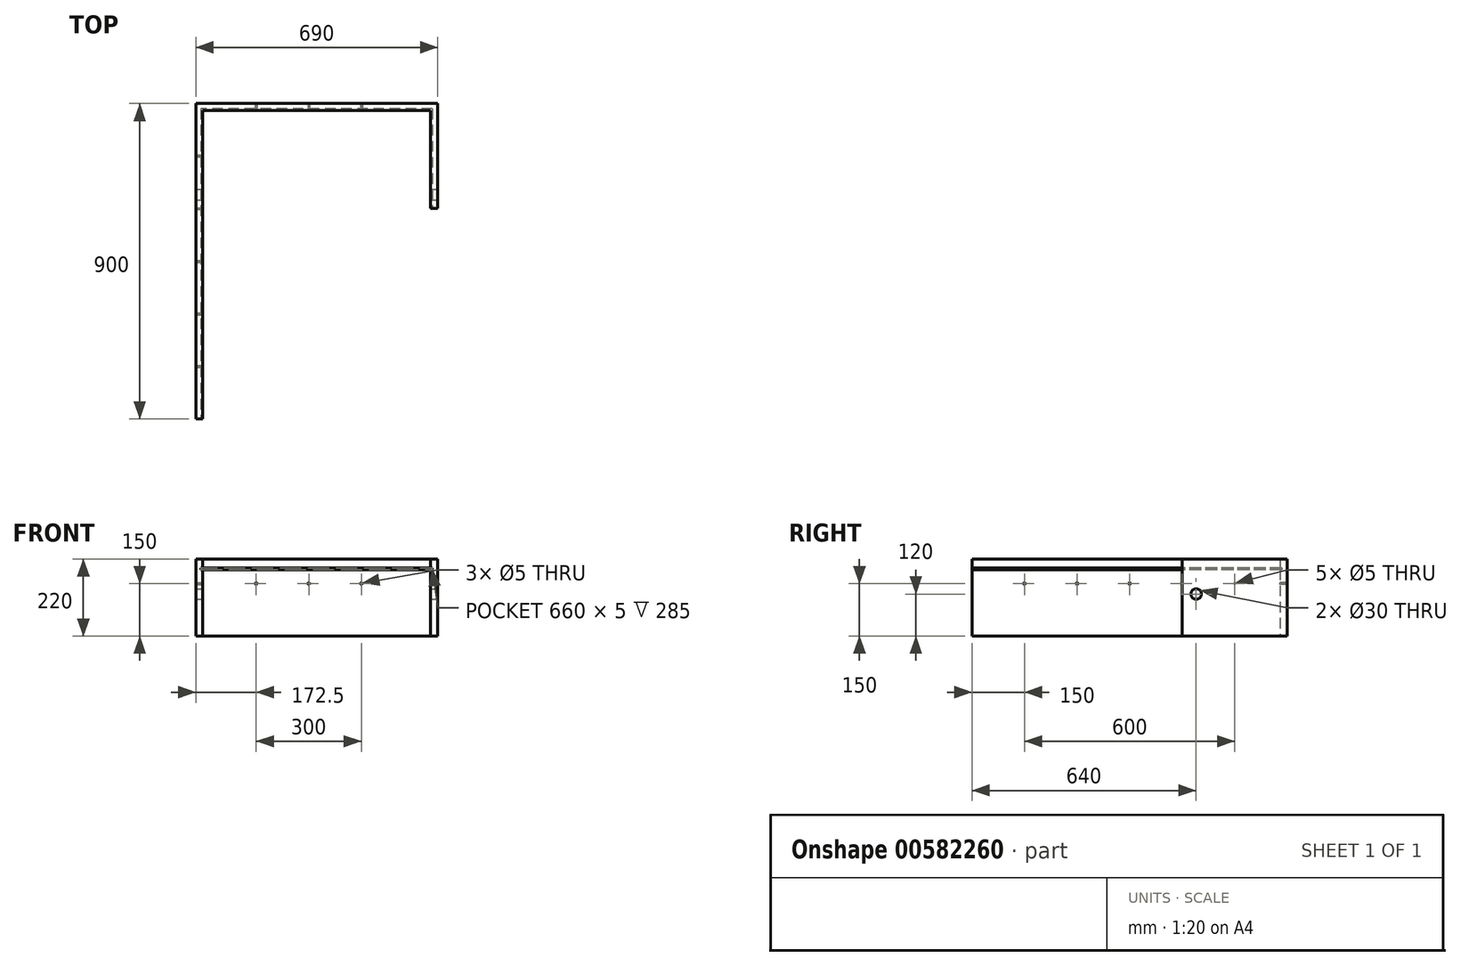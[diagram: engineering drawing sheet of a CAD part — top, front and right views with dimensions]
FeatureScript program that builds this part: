
annotation { "Feature Type Name" : "Feature", "Feature Type Description" : "" }
export const myFeature = defineFeature(function(context is Context, id is Id, definition is map)
    precondition{}
    {
        {
            var Q0;
            Q0=qCreatedBy(makeId("Top.planeOp"),FACE);
            var sketch = newSketch(context, id + "F0", { "sketchPlane" : qUnion([Q0])});
            skLineSegment(sketch, "E0.bottom", {"start": v(-325, -450) * mm, "end": v(-345, -450) * mm});
            skLineSegment(sketch, "E0.top", {"start": v(345, 450) * mm, "end": v(-345, 450) * mm});
            skLineSegment(sketch, "E0.left", {"start": v(345, 150) * mm, "end": v(345, 450) * mm});
            skLineSegment(sketch, "E0.right", {"start": v(-345, -450) * mm, "end": v(-345, 450) * mm});
            skPoint(sketch, "E0.middle", {"position": v(0, 0) * mm});
            skLineSegment(sketch, "E1.bottom", {"start": v(325, 430) * mm, "end": v(-325, 430) * mm});
            skLineSegment(sketch, "E1.left", {"start": v(325, 430) * mm, "end": v(325, 150) * mm});
            skLineSegment(sketch, "E1.right", {"start": v(-325, 430) * mm, "end": v(-325, -430) * mm});
            skLineSegment(sketch, "E2", {"start": v(345, 150) * mm, "end": v(325, 150) * mm});
            skLineSegment(sketch, "E3", {"start": v(-325, -430) * mm, "end": v(-325, -450) * mm});
            skSolve(sketch);
        }
        {
            var Q0;
            Q0=makeQuery(id+"F0.imprint","IMPRINT",FACE,{"disambiguationData":[TD([[makeQuery(id+"F0.imprint","IMPRINT",EDGE,{"derivedFrom":sQuery(id+"F0.wireOp",EDGE,"E0.bottom")}),-1.0]])]});
            extrude(context, id + "F1", {"entities" : qUnion([Q0]), "depth" : 220 * mm, "offsetDistance" : 25 * mm});
        }
        {
            var Q0;
            Q0=makeQuery(id+"F1.opExtrude","SWEPT_FACE",FACE,{"disambiguationData":[OSD([sQuery(id+"F0.wireOp",EDGE,"E0.bottom")])]});
            var sketch = newSketch(context, id + "F2", { "sketchPlane" : qUnion([Q0])});
            skLineSegment(sketch, "E4.bottom", {"start": v(-325, 195) * mm, "end": v(-330, 195) * mm});
            skLineSegment(sketch, "E4.top", {"start": v(-325, 190) * mm, "end": v(-330, 190) * mm});
            skLineSegment(sketch, "E4.left", {"start": v(-325, 195) * mm, "end": v(-325, 190) * mm});
            skLineSegment(sketch, "E4.right", {"start": v(-330, 195) * mm, "end": v(-330, 190) * mm});
            skSolve(sketch);
        }
        {
            var Q0;
            Q0 = qSketchRegion(id + "F2", true);
            extrude(context, id + "F3", {"entities" : qUnion([Q0]), "operationType" : NewBodyOperationType.REMOVE, "oppositeDirection" : true, "depth" : 885 * mm, "offsetDistance" : 25 * mm});
        }
        {
            var Q0;
            Q0=makeQuery(id+"F1.opExtrude","SWEPT_FACE",FACE,{"disambiguationData":[OSD([sQuery(id+"F0.wireOp",EDGE,"E1.bottom")])]});
            var sketch = newSketch(context, id + "F4", { "sketchPlane" : qUnion([Q0])});
            skLineSegment(sketch, "E5.bottom", {"start": v(-325, 195) * mm, "end": v(325, 195) * mm});
            skLineSegment(sketch, "E5.top", {"start": v(-325, 190) * mm, "end": v(325, 190) * mm});
            skLineSegment(sketch, "E5.left", {"start": v(-325, 195) * mm, "end": v(-325, 190) * mm});
            skLineSegment(sketch, "E5.right", {"start": v(325, 195) * mm, "end": v(325, 190) * mm});
            skSolve(sketch);
        }
        {
            var Q0;
            Q0=makeQuery(id+"F4.imprint","IMPRINT",FACE,{"disambiguationData":[TD([[makeQuery(id+"F4.imprint","IMPRINT",EDGE,{"derivedFrom":sQuery(id+"F4.wireOp",EDGE,"E5.bottom")}),-1.0]])]});
            extrude(context, id + "F5", {"entities" : qUnion([Q0]), "operationType" : NewBodyOperationType.REMOVE, "oppositeDirection" : true, "depth" : 5 * mm, "offsetDistance" : 25 * mm});
        }
        {
            var Q0;
            Q0=makeQuery(id+"F1.opExtrude","SWEPT_FACE",FACE,{"disambiguationData":[OSD([sQuery(id+"F0.wireOp",EDGE,"E2")])]});
            var sketch = newSketch(context, id + "F6", { "sketchPlane" : qUnion([Q0])});
            skLineSegment(sketch, "E6.bottom", {"start": v(325, 195) * mm, "end": v(330, 195) * mm});
            skLineSegment(sketch, "E6.top", {"start": v(325, 190) * mm, "end": v(330, 190) * mm});
            skLineSegment(sketch, "E6.left", {"start": v(325, 195) * mm, "end": v(325, 190) * mm});
            skLineSegment(sketch, "E6.right", {"start": v(330, 195) * mm, "end": v(330, 190) * mm});
            skSolve(sketch);
        }
        {
            var Q0;
            Q0 = qSketchRegion(id + "F6", true);
            extrude(context, id + "F7", {"entities" : qUnion([Q0]), "operationType" : NewBodyOperationType.REMOVE, "oppositeDirection" : true, "depth" : 285 * mm, "offsetDistance" : 25 * mm});
        }
        {
            var Q0;
            Q0=makeQuery(id+"F1.opExtrude","SWEPT_FACE",FACE,{"disambiguationData":[OSD([sQuery(id+"F0.wireOp",EDGE,"E0.left")])]});
            var sketch = newSketch(context, id + "F8", { "sketchPlane" : qUnion([Q0])});
            skCircle(sketch, "E7", {"center": v(190, 120) * mm, "radius": 15 * mm});
            skSolve(sketch);
        }
        {
            var Q0;
            Q0 = qSketchRegion(id + "F8", true);
            extrude(context, id + "F9", {"entities" : qUnion([Q0]), "operationType" : NewBodyOperationType.REMOVE, "oppositeDirection" : true, "depth" : 800 * mm, "offsetDistance" : 25 * mm});
        }
        {
            var Q0;
            {var subQ1=sQuery(id+"F0.wireOp",EDGE,"E3");var subQ2=sQuery(id+"F0.wireOp",EDGE,"E1.right");Q0=makeQuery(id+"F3.boolean.opBoolean","SPLIT",FACE,{"disambiguationData":[TD([makeQuery(id+"F3.opExtrude","SWEPT_FACE",FACE,{"disambiguationData":[OSD([sQuery(id+"F2.wireOp",EDGE,"E4.top")])]})])],"derivedFrom":makeQuery(id+"F1.opExtrude","SWEPT_FACE",FACE,{"disambiguationData":[OSD([subQ2,subQ1])]})});}
            var sketch = newSketch(context, id + "F10", { "sketchPlane" : qUnion([Q0])});
            skCircle(sketch, "E8", {"center": v(-300, 150) * mm, "radius": 2.5 * mm});
            skCircle(sketch, "E9.1.0.0", {"center": v(-150, 150) * mm, "radius": 2.5 * mm});
            skCircle(sketch, "E9.2.0.0", {"center": v(0, 150) * mm, "radius": 2.5 * mm});
            skCircle(sketch, "E9.3.0.0", {"center": v(150, 150) * mm, "radius": 2.5 * mm});
            skCircle(sketch, "E9.4.0.0", {"center": v(300, 150) * mm, "radius": 2.5 * mm});
            skLineSegment(sketch, "E9.direction1", {"start": v(-300, 150) * mm, "end": v(-150, 150) * mm, "construction": true});
            skSolve(sketch);
        }
        {
            var Q0;
            Q0 = qSketchRegion(id + "F10", true);
            extrude(context, id + "F11", {"entities" : qUnion([Q0]), "operationType" : NewBodyOperationType.REMOVE, "oppositeDirection" : true, "depth" : 25 * mm, "offsetDistance" : 25 * mm});
        }
        {
            var Q0;
            {var subQ3=sQuery(id+"F0.wireOp",EDGE,"E1.bottom");Q0=makeQuery(id+"F5.boolean.opBoolean","SPLIT",FACE,{"disambiguationData":[TD([makeQuery(id+"F3.boolean.opBoolean","COPY",FACE,{"derivedFrom":makeQuery(id+"F3.opExtrude","SWEPT_FACE",FACE,{"disambiguationData":[OSD([sQuery(id+"F2.wireOp",EDGE,"E4.top")])]})})])],"derivedFrom":makeQuery(id+"F1.opExtrude","SWEPT_FACE",FACE,{"disambiguationData":[OSD([subQ3])]})});}
            var sketch = newSketch(context, id + "F12", { "sketchPlane" : qUnion([Q0])});
            skCircle(sketch, "E10", {"center": v(-172.5, 150) * mm, "radius": 2.5 * mm});
            skCircle(sketch, "E11.1.0.0", {"center": v(-22.5, 150) * mm, "radius": 2.5 * mm});
            skCircle(sketch, "E11.2.0.0", {"center": v(127.5, 150) * mm, "radius": 2.5 * mm});
            skLineSegment(sketch, "E11.direction1", {"start": v(-172.5, 150) * mm, "end": v(-22.5, 150) * mm, "construction": true});
            skSolve(sketch);
        }
        {
            var Q0;
            Q0 = qSketchRegion(id + "F12", true);
            extrude(context, id + "F13", {"entities" : qUnion([Q0]), "operationType" : NewBodyOperationType.REMOVE, "oppositeDirection" : true, "depth" : 25 * mm, "offsetDistance" : 25 * mm});
        }
    });
